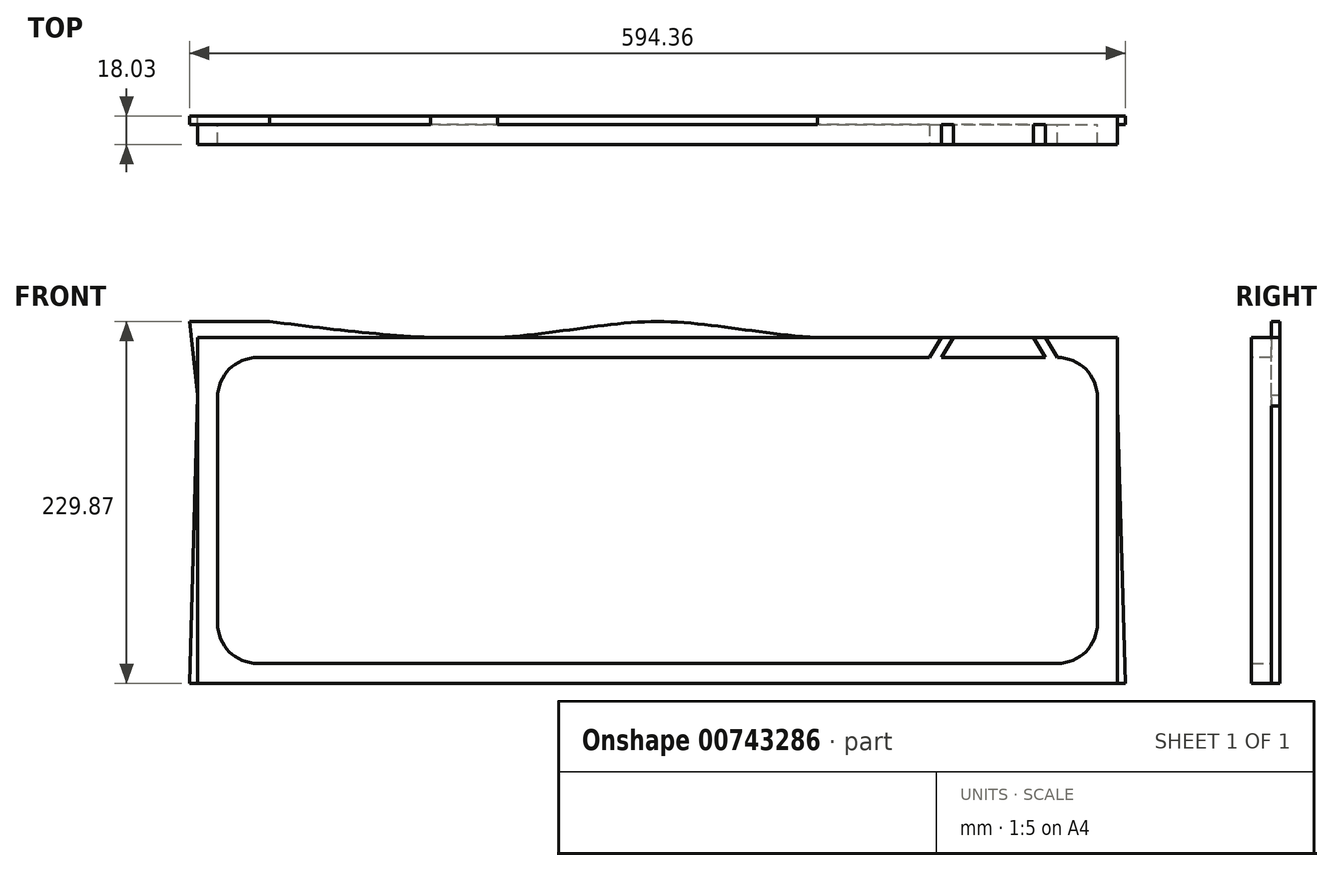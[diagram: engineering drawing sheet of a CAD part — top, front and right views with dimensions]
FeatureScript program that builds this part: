
annotation { "Feature Type Name" : "Feature", "Feature Type Description" : "" }
export const myFeature = defineFeature(function(context is Context, id is Id, definition is map)
    precondition{}
    {
        {
            var Q0;
            Q0=qCreatedBy(makeId("Front.planeOp"),FACE);
            var sketch = newSketch(context, id + "F0", { "sketchPlane" : qUnion([Q0])});
            skLineSegment(sketch, "E0.bottom", {"start": v(0, 0) * mm, "end": v(-584.2, 0) * mm});
            skLineSegment(sketch, "E0.top", {"start": v(0, 219.7) * mm, "end": v(-584.2, 219.7) * mm});
            skLineSegment(sketch, "E0.left", {"start": v(0, 0) * mm, "end": v(0, 219.7) * mm});
            skLineSegment(sketch, "E0.right", {"start": v(-584.2, 0) * mm, "end": v(-584.2, 219.7) * mm});
            skPoint(sketch, "E1", {"position": v(-292.1, 219.7) * mm});
            skSolve(sketch);
        }
        {
            var Q0;
            Q0=makeQuery(id+"F0.imprint","IMPRINT",FACE,{"disambiguationData":[TD([[makeQuery(id+"F0.imprint","IMPRINT",EDGE,{"derivedFrom":sQuery(id+"F0.wireOp",EDGE,"E0.bottom")}),-1.0]])]});
            extrude(context, id + "F1", {"entities" : qUnion([Q0]), "depth" : 5.33 * mm});
        }
        {
            var Q0;
            Q0=makeQuery(id+"F1.opExtrude","CAP_FACE",FACE,{"disambiguationData":[OSD([sQuery(id+"F0.wireOp",EDGE,"E0.bottom"),sQuery(id+"F0.wireOp",EDGE,"E0.top"),sQuery(id+"F0.wireOp",EDGE,"E0.left"),sQuery(id+"F0.wireOp",EDGE,"E0.right")])],"isStart":false});
            var sketch = newSketch(context, id + "F2", { "sketchPlane" : qUnion([Q0])});
            skLineSegment(sketch, "E2", {"start": v(-6.35, 219.71) * mm, "end": v(-577.85, 219.7) * mm});
            skLineSegment(sketch, "E3", {"start": v(-571.5, 207) * mm, "end": v(-571.5, 12.7) * mm});
            skLineSegment(sketch, "E4", {"start": v(-571.5, 12.7) * mm, "end": v(-12.7, 12.7) * mm});
            skLineSegment(sketch, "E5", {"start": v(-12.7, 12.7) * mm, "end": v(-12.7, 207) * mm});
            skLineSegment(sketch, "E6", {"start": v(-12.7, 207.01) * mm, "end": v(-571.5, 207) * mm});
            skSolve(sketch);
        }
        {
            var Q0;
            Q0=makeQuery(id+"F2.imprint","IMPRINT",FACE,{"disambiguationData":[TD([[makeQuery(id+"F2.imprint","IMPRINT",EDGE,{"derivedFrom":sQuery(id+"F2.wireOp",EDGE,"0a8MKLZ5-oheQ-0zMi-XPoK-jZ4sBujb71DH")}),1.0]])]});
            var Q1;
            {var subQ0=sQuery(id+"F2.wireOp",EDGE,"E2");Q1=makeQuery(id+"F2.imprint","IMPRINT",FACE,{"disambiguationData":[TD([[makeQuery(id+"F2.imprint","IMPRINT",EDGE,{"derivedFrom":subQ0}),1.0]])]});}
            extrude(context, id + "F3", {"entities" : qUnion([Q0, Q1]), "operationType" : NewBodyOperationType.ADD, "depth" : 12.7 * mm, "offsetDistance" : 25.4 * mm});
        }
        {
            var Q0;
            Q0=makeQuery(id+"F3.opExtrude","SWEPT_EDGE",EDGE,{"disambiguationData":[OSD([sQuery(id+"F2.wireOp",EDGE,"E3"),sQuery(id+"F2.wireOp",EDGE,"E6")])]});
            var Q1;
            Q1=makeQuery(id+"F3.opExtrude","SWEPT_EDGE",EDGE,{"disambiguationData":[OSD([sQuery(id+"F2.wireOp",EDGE,"E5"),sQuery(id+"F2.wireOp",EDGE,"E6")])]});
            var Q2;
            Q2=makeQuery(id+"F3.opExtrude","SWEPT_EDGE",EDGE,{"disambiguationData":[OSD([sQuery(id+"F2.wireOp",EDGE,"E4"),sQuery(id+"F2.wireOp",EDGE,"E5")])]});
            var Q3;
            Q3=makeQuery(id+"F3.opExtrude","SWEPT_EDGE",EDGE,{"disambiguationData":[OSD([sQuery(id+"F2.wireOp",EDGE,"E3"),sQuery(id+"F2.wireOp",EDGE,"E4")])]});
            fillet(context, id + "F4", {"entities" : qUnion([Q0, Q1, Q2, Q3]), "radius" : 25.4 * mm, "tangentPropagation" : true, "allowEdgeOverflow" : false});
        }
        {
            var Q0;
            Q0=makeQuery(id+"F3.opExtrude","CAP_FACE",FACE,{"disambiguationData":[OSD([sQuery(id+"F2.wireOp",EDGE,"0a8MKLZ5-oheQ-0zMi-XPoK-jZ4sBujb71DH"),sQuery(id+"F2.wireOp",EDGE,"1G2fN8Fc-beI2-8vQH-utY2-EfryYqRfW7gx"),sQuery(id+"F2.wireOp",EDGE,"ED9PZ5wW-gA8i-4lJh-uNFJ-W9pF7rNdlAKq"),sQuery(id+"F2.wireOp",EDGE,"E2"),sQuery(id+"F2.wireOp",EDGE,"E3"),sQuery(id+"F2.wireOp",EDGE,"E4"),sQuery(id+"F2.wireOp",EDGE,"E5"),sQuery(id+"F2.wireOp",EDGE,"E6")])],"isStart":false});
            var sketch = newSketch(context, id + "F5", { "sketchPlane" : qUnion([Q0])});
            skPoint(sketch, "E7", {"position": v(-111.76, 219.7) * mm});
            skPoint(sketch, "E8", {"position": v(-104.14, 219.7) * mm});
            skPoint(sketch, "E9", {"position": v(-53.34, 219.7) * mm});
            skPoint(sketch, "E10", {"position": v(-45.72, 219.7) * mm});
            skPoint(sketch, "E11", {"position": v(-376.28, 272.75) * mm});
            skPoint(sketch, "E12", {"position": v(-12.7, 0) * mm});
            skPoint(sketch, "E13", {"position": v(-20.32, 0) * mm});
            skLineSegment(sketch, "E14", {"start": v(-20.32, 0) * mm, "end": v(-12.7, 0) * mm});
            skPoint(sketch, "E15", {"position": v(-111.76, 207.01) * mm});
            skPoint(sketch, "E16", {"position": v(-119.38, 207.01) * mm});
            skLineSegment(sketch, "E17", {"start": v(-119.38, 207.01) * mm, "end": v(-111.76, 219.7) * mm});
            skLineSegment(sketch, "E18", {"start": v(-119.38, 207.01) * mm, "end": v(-111.76, 207.01) * mm});
            skLineSegment(sketch, "E19", {"start": v(-111.76, 207.01) * mm, "end": v(-104.14, 219.7) * mm});
            skLineSegment(sketch, "E20", {"start": v(-111.76, 219.7) * mm, "end": v(-104.14, 219.7) * mm});
            skLineSegment(sketch, "E21", {"start": v(-53.34, 219.7) * mm, "end": v(-45.72, 219.7) * mm});
            skLineSegment(sketch, "E22", {"start": v(-104.14, 219.7) * mm, "end": v(-53.34, 219.7) * mm});
            skLineSegment(sketch, "E23", {"start": v(-53.34, 219.7) * mm, "end": v(-104.14, 219.7) * mm});
            skLineSegment(sketch, "E24", {"start": v(-104.14, 219.7) * mm, "end": v(-107.23, 214.56) * mm});
            skPoint(sketch, "E25", {"position": v(-38.1, 207.01) * mm});
            skPoint(sketch, "E26", {"position": v(-45.72, 207.01) * mm});
            skLineSegment(sketch, "E27", {"start": v(-53.34, 219.7) * mm, "end": v(-45.72, 207.01) * mm});
            skLineSegment(sketch, "E28", {"start": v(-45.72, 219.7) * mm, "end": v(-38.1, 207.01) * mm});
            skLineSegment(sketch, "E29", {"start": v(-45.72, 207.01) * mm, "end": v(-38.1, 207.01) * mm});
            skLineSegment(sketch, "E30", {"start": v(-45.72, 219.7) * mm, "end": v(-53.34, 219.7) * mm});
            skPoint(sketch, "E31", {"position": v(-50.25, 214.56) * mm});
            skLineSegment(sketch, "E32", {"start": v(-107.23, 214.56) * mm, "end": v(-50.25, 214.56) * mm});
            skSolve(sketch);
        }
        {
            var Q0;
            Q0=makeQuery(id+"F5.imprint","IMPRINT",FACE,{"disambiguationData":[TD([[makeQuery(id+"F5.imprint","IMPRINT",EDGE,{"derivedFrom":sQuery(id+"F5.wireOp",EDGE,"E17")}),-1.0]])]});
            var Q1;
            {var subQ8=sQuery(id+"F5.wireOp",EDGE,"RZINdJYM-ykuw-GilU-JIjt-DnibDYUsXZuo");Q1=makeQuery(id+"F5.imprint","IMPRINT",FACE,{"disambiguationData":[TD([[makeQuery(id+"F5.imprint","IMPRINT",EDGE,{"derivedFrom":subQ8}),1.0]])]});}
            var Q2;
            Q2=makeQuery(id+"F5.imprint","IMPRINT",FACE,{"disambiguationData":[TD([[makeQuery(id+"F5.imprint","IMPRINT",EDGE,{"derivedFrom":sQuery(id+"F5.wireOp",EDGE,"RZINdJYM-ykuw-GilU-JIjt-DnibDYUsXZuo")}),-1.0]])]});
            var Q3;
            Q3=makeQuery(id+"F5.imprint","IMPRINT",FACE,{"disambiguationData":[TD([[makeQuery(id+"F5.imprint","IMPRINT",EDGE,{"derivedFrom":sQuery(id+"F5.wireOp",EDGE,"NQJIxGkc-Vixr-o2zM-VUe3-bVQ5EoZFKsab")}),1.0]])]});
            var Q4;
            Q4=makeQuery(id+"F5.imprint","IMPRINT",FACE,{"disambiguationData":[TD([[makeQuery(id+"F5.imprint","IMPRINT",EDGE,{"derivedFrom":sQuery(id+"F5.wireOp",EDGE,"E27")}),1.0]])]});
            var Q5;
            {var subQ0=sQuery(id+"F5.wireOp",EDGE,"E23");Q5=makeQuery(id+"F5.imprint","IMPRINT",FACE,{"disambiguationData":[TD([[makeQuery(id+"F5.imprint","IMPRINT",EDGE,{"derivedFrom":subQ0}),1.0]])]});}
            extrude(context, id + "F6", {"entities" : qUnion([Q0, Q1, Q2, Q3, Q4, Q5]), "operationType" : NewBodyOperationType.REMOVE, "oppositeDirection" : true, "depth" : 12.7 * mm});
        }
        {
            var Q0;
            Q0=makeQuery(id+"F1.opExtrude","CAP_FACE",FACE,{"disambiguationData":[OSD([sQuery(id+"F0.wireOp",EDGE,"E0.bottom"),sQuery(id+"F0.wireOp",EDGE,"E0.top"),sQuery(id+"F0.wireOp",EDGE,"E0.left"),sQuery(id+"F0.wireOp",EDGE,"E0.right")])],"isStart":true});
            var sketch = newSketch(context, id + "F7", { "sketchPlane" : qUnion([Q0])});
            skLineSegment(sketch, "E33", {"start": v(0, 0) * mm, "end": v(-5.08, 0) * mm});
            skLineSegment(sketch, "E34", {"start": v(-5.08, 0) * mm, "end": v(-5.08, 229.87) * mm});
            skLineSegment(sketch, "E35", {"start": v(-5.08, 229.87) * mm, "end": v(589.28, 229.87) * mm});
            skLineSegment(sketch, "E36", {"start": v(589.28, 229.87) * mm, "end": v(589.28, 0) * mm});
            skLineSegment(sketch, "E37", {"start": v(589.28, 0) * mm, "end": v(584.2, 0) * mm});
            skPoint(sketch, "E38", {"position": v(589.28, 114.93) * mm});
            skPoint(sketch, "E39", {"position": v(584.2, 109.85) * mm});
            skPoint(sketch, "E40", {"position": v(292.1, 229.87) * mm});
            skPoint(sketch, "E41", {"position": v(292.1, 219.7) * mm});
            skPoint(sketch, "E42", {"position": v(-5.08, 114.93) * mm});
            skPoint(sketch, "E43", {"position": v(0, 109.85) * mm});
            skPoint(sketch, "E44", {"position": v(538.48, 229.87) * mm});
            skPoint(sketch, "E45", {"position": v(45.72, 229.87) * mm});
            skPoint(sketch, "E46", {"position": v(-5.08, 191.77) * mm});
            skPoint(sketch, "E47", {"position": v(589.28, 191.77) * mm});
            skPoint(sketch, "E48", {"position": v(584.2, 183.25) * mm});
            skPoint(sketch, "E49", {"position": v(0, 176.13) * mm});
            skPoint(sketch, "E50", {"position": v(589.28, 63.5) * mm});
            skPoint(sketch, "E51", {"position": v(-5.08, 63.5) * mm});
            skPoint(sketch, "E52", {"position": v(0, 219.7) * mm});
            skPoint(sketch, "E53", {"position": v(584.2, 219.7) * mm});
            skPoint(sketch, "E54", {"position": v(393.7, 219.7) * mm});
            skPoint(sketch, "E55", {"position": v(190.5, 219.7) * mm});
            skFitSpline(sketch, "E56", {"points": [v(538.48, 229.87) * mm, v(393.7, 219.7) * mm, v(292.1, 229.87) * mm, v(190.5, 219.7) * mm, v(45.72, 229.87) * mm], "startDerivative": vector(-556.08, -69.34) * mm, "endDerivative": vector(-556.08, 69.34) * mm});
            skLineSegment(sketch, "E57", {"start": v(-5.08, 229.87) * mm, "end": v(0, 176.13) * mm});
            skLineSegment(sketch, "E58", {"start": v(584.2, 183.25) * mm, "end": v(589.28, 229.87) * mm});
            skLineSegment(sketch, "E59", {"start": v(-5.08, 0) * mm, "end": v(0, 176.13) * mm});
            skLineSegment(sketch, "E60", {"start": v(584.2, 183.25) * mm, "end": v(589.28, 0) * mm});
            skSolve(sketch);
        }
        {
            var Q0;
            {var subQ3=sQuery(id+"F7.wireOp",EDGE,"1cZOkDzA-QB0z-r1xi-g2sP-Uw8mw8TRGHdY");Q0=makeQuery(id+"F7.imprint","IMPRINT",FACE,{"disambiguationData":[TD([[makeQuery(id+"F7.imprint","IMPRINT",EDGE,{"derivedFrom":subQ3}),-1.0]])]});}
            var Q1;
            {var subQ0=sQuery(id+"F7.wireOp",EDGE,"E56");var subQ1=makeQuery(id+"F7.imprint","INTERSECT",VERTEX,{"disambiguationData":[OD(2.0)],"derivedFrom":[sQuery(id+"F7.wireOp",EDGE,"E35"),subQ0]});Q1=makeQuery(id+"F7.imprint","IMPRINT",FACE,{"disambiguationData":[TD([[makeQuery(id+"F7.imprint","IMPRINT",EDGE,{"disambiguationData":[TD([[subQ1,1.0]])],"derivedFrom":subQ0}),1.0]])]});}
            var Q2;
            {var subQ1=sQuery(id+"F7.wireOp",EDGE,"E35");var subQ7=sQuery(id+"F7.wireOp",EDGE,"E56");var subQ8=makeQuery(id+"F7.imprint","INTERSECT",VERTEX,{"disambiguationData":[OD(1.0)],"derivedFrom":[subQ1,subQ7]});Q2=makeQuery(id+"F7.imprint","IMPRINT",FACE,{"disambiguationData":[TD([[makeQuery(id+"F7.imprint","IMPRINT",EDGE,{"disambiguationData":[TD([[subQ8,1.0]])],"derivedFrom":subQ7}),1.0]])]});}
            var Q3;
            {var subQ0=sQuery(id+"F7.wireOp",EDGE,"E37");Q3=makeQuery(id+"F7.imprint","IMPRINT",FACE,{"disambiguationData":[TD([[makeQuery(id+"F7.imprint","IMPRINT",EDGE,{"derivedFrom":subQ0}),-1.0]])]});}
            var Q4;
            {var subQ7=sQuery(id+"F7.wireOp",EDGE,"E58");Q4=makeQuery(id+"F7.imprint","IMPRINT",FACE,{"disambiguationData":[TD([[makeQuery(id+"F7.imprint","IMPRINT",EDGE,{"derivedFrom":subQ7}),1.0]])]});}
            var Q5;
            {var subQ0=sQuery(id+"F7.wireOp",EDGE,"E33");Q5=makeQuery(id+"F7.imprint","IMPRINT",FACE,{"disambiguationData":[TD([[makeQuery(id+"F7.imprint","IMPRINT",EDGE,{"derivedFrom":subQ0}),-1.0]])]});}
            extrude(context, id + "F8", {"entities" : qUnion([Q0, Q1, Q2, Q3, Q4, Q5]), "operationType" : NewBodyOperationType.ADD, "depth" : -5.33 * mm});
        }
    });
